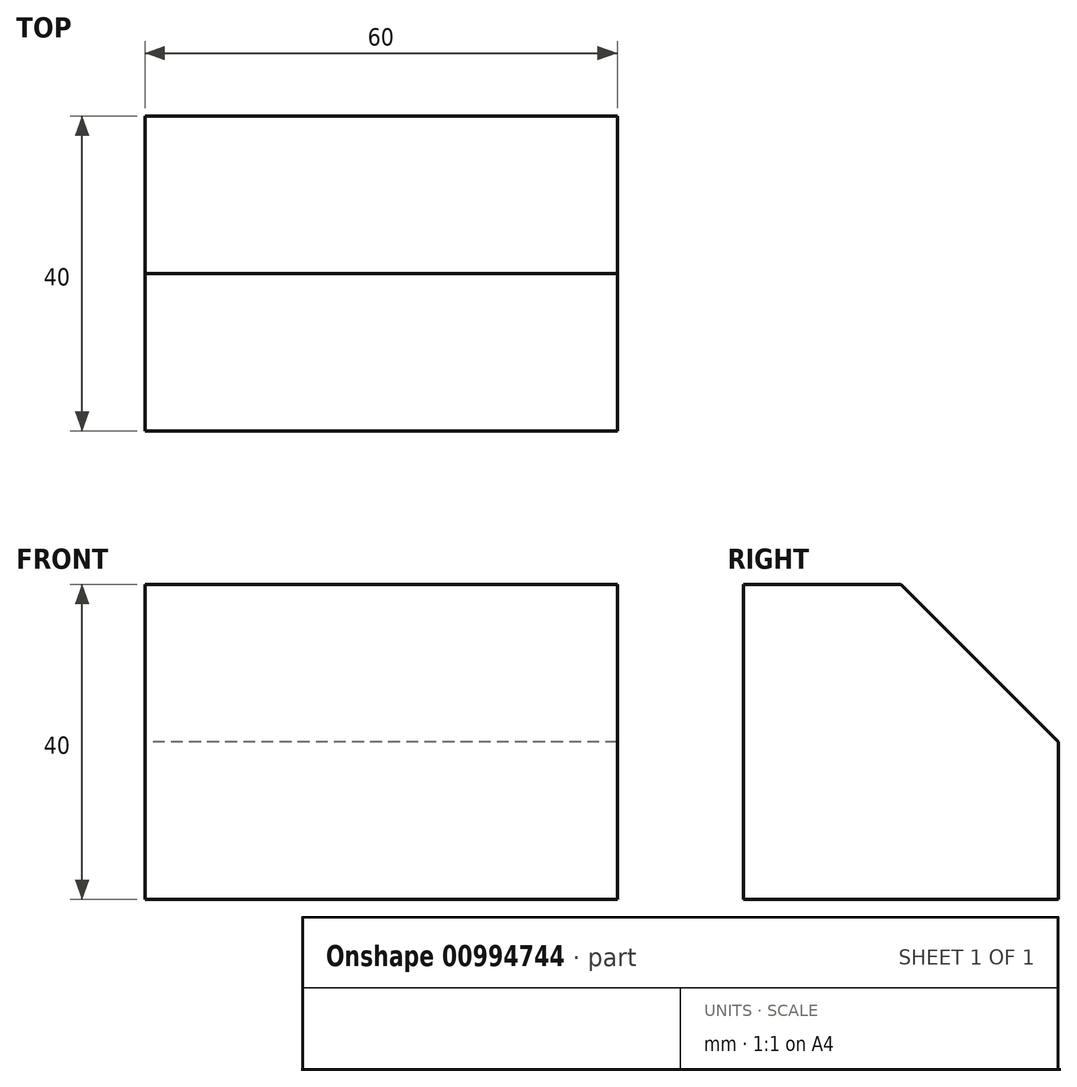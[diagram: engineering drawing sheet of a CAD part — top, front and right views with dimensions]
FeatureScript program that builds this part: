
annotation { "Feature Type Name" : "Feature", "Feature Type Description" : "" }
export const myFeature = defineFeature(function(context is Context, id is Id, definition is map)
    precondition{}
    {
        {
            var Q0;
            Q0=qCreatedBy(makeId("Right.planeOp"),FACE);
            var sketch = newSketch(context, id + "F0", { "sketchPlane" : qUnion([Q0])});
            skLineSegment(sketch, "E0", {"start": v(-20, 20) * mm, "end": v(0, 20) * mm});
            skLineSegment(sketch, "E1", {"start": v(0, 20) * mm, "end": v(20, 0) * mm});
            skLineSegment(sketch, "E2", {"start": v(20, 0) * mm, "end": v(20, -20) * mm});
            skLineSegment(sketch, "E3", {"start": v(20, -20) * mm, "end": v(-20, -20) * mm});
            skLineSegment(sketch, "E4", {"start": v(-20, -20) * mm, "end": v(-20, 20) * mm});
            skSolve(sketch);
        }
        {
            var Q0;
            Q0 = qSketchRegion(id + "F0", true);
            extrude(context, id + "F1", {"entities" : qUnion([Q0]), "endBound" : BoundingType.SYMMETRIC, "depth" : 60 * mm, "offsetDistance" : 25 * mm});
        }
    });
